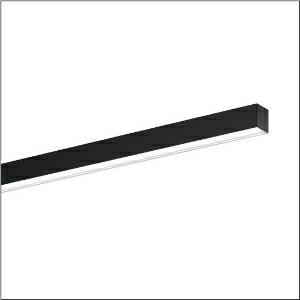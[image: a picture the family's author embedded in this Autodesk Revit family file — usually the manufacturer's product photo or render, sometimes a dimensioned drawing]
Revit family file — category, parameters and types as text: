
# Revit family: silica_r__21_51mx20dc35bb_a1de
name_source: partatom
category: Lighting Fixtures
units: mm (PartAtom-declared; Revit-internal decimal feet)

## family parameters
Cut with Voids When Loaded = No
Host = Face
Light Source = No
Part Type = Normal
Room Calculation Point = No
Round Connector Dimension = Use Diameter
Shared = No

## types (1)
- --- (1 x LED, 6000 lm, 42.6 W, 3000K)
    Apparent Load = 43 VA
    CIE Flux Codes = 48 79 96 100 100
    Color Rendering = 80
    Color Temperature = 3000K
    Default Elevation = 1800 mm
    Description = Silica® 21, office luminaire, primary optical cover: cover, of PMMA, opal, light emission: direct distribution, primary light characteristic: symmetric, installation type: surface-mounted, LED, rated luminous flux: 6.000lm, luminous efficacy: 141lm/W, light colour: 830, colour temperature: 3000K, control gear: DALI 2, with terminal, 3+2-pole, max. 2.5mm², mains connection: 220..240V, AC, 50/60Hz, rated input power: 42.6W, luminaire housing, of aluminium, matt jet black (RAL 9005), length: 3.004mm, width: 53mm, height: 53mm, protection rating (complete): IP20, insulation class (complete): insulation class I (protective earthing), certification: CE, permissible operating ambient temperature: 0..+35°C, standard: EN 50419, packaging unit: 1 piece
    Height = 53 mm
    Lamp = 1 x LED
    Lamp Light Flux = 6000 lm
    Lamp Power = 42.6 W
    Lamp count = 1
    Length = 3004 mm
    Luminous efficacy = 141 lm/W
    Manufacturer = Siteco
    ModVariant = No
    Model = 51MX20DC35BB
    Mounting Place = Ceiling
    Mounting Type = Surface mounted
    Number of Poles = 1
    OnlyDefault = Yes
    Power Factor = 1
    Product Name = Silica® 21
    Product group = office luminaire | ceiling mounted
    ProductGroupID = 302
    Protection Class = Protection class I
    Protection Degree = IP 20
    RLX_Detail_Level = 1
    RLX_Emergency_Light_Flux = 0 lm
    RLX_Emergency_Type = 0
    RLX_Emergency_Type_DB = No
    RlxData = <blob elided: 28905 chars, md5=b8eead33>
    Socket = socket
    Standby Power = 0 W
    System Light Flux = 6000 lm
    System Power = 43 W
    Type Comments = factory setting: luminous flux: 100 % | dim-lin: 254 | 233 mA
    Type Image = l_1335925.jpg
    URL = http://relux.com
    VarID = @adj_117802
    Voltage = 0 V
    Weight = 0.00 kg
    Width = 53 mm

## geometry (parser evidence)
native form markers: Blend x4, Sweep x10
no freeform markers — native parametric forms only
